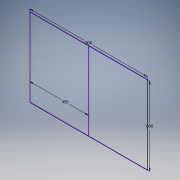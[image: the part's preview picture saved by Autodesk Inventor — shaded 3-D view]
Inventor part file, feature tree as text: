
AUTODESK INVENTOR PART (.ipt)
format: ipt  version: 2019 (Build 230136000, 136)  size: 159,232 bytes
history: native  units: mm
features: extrude x2, sketch x2, other x1, projected_geometry x1
ambient origin geometry x8: Origin, YZ Plane, XZ Plane, XY Plane, X Axis, Y Axis, Z Axis, Center Point
bodies: Body1 (feature_tree)
feature tree (6):
  other  "Твердое тело1"
  extrude  "Выдавливание1"  Depth=900.0mm
  extrude  "Выдавливание2"  Depth=600.0mm
  sketch  "Эскиз1"
  sketch  "Эскиз2"
  projected_geometry  "Спроецированная петля1"
